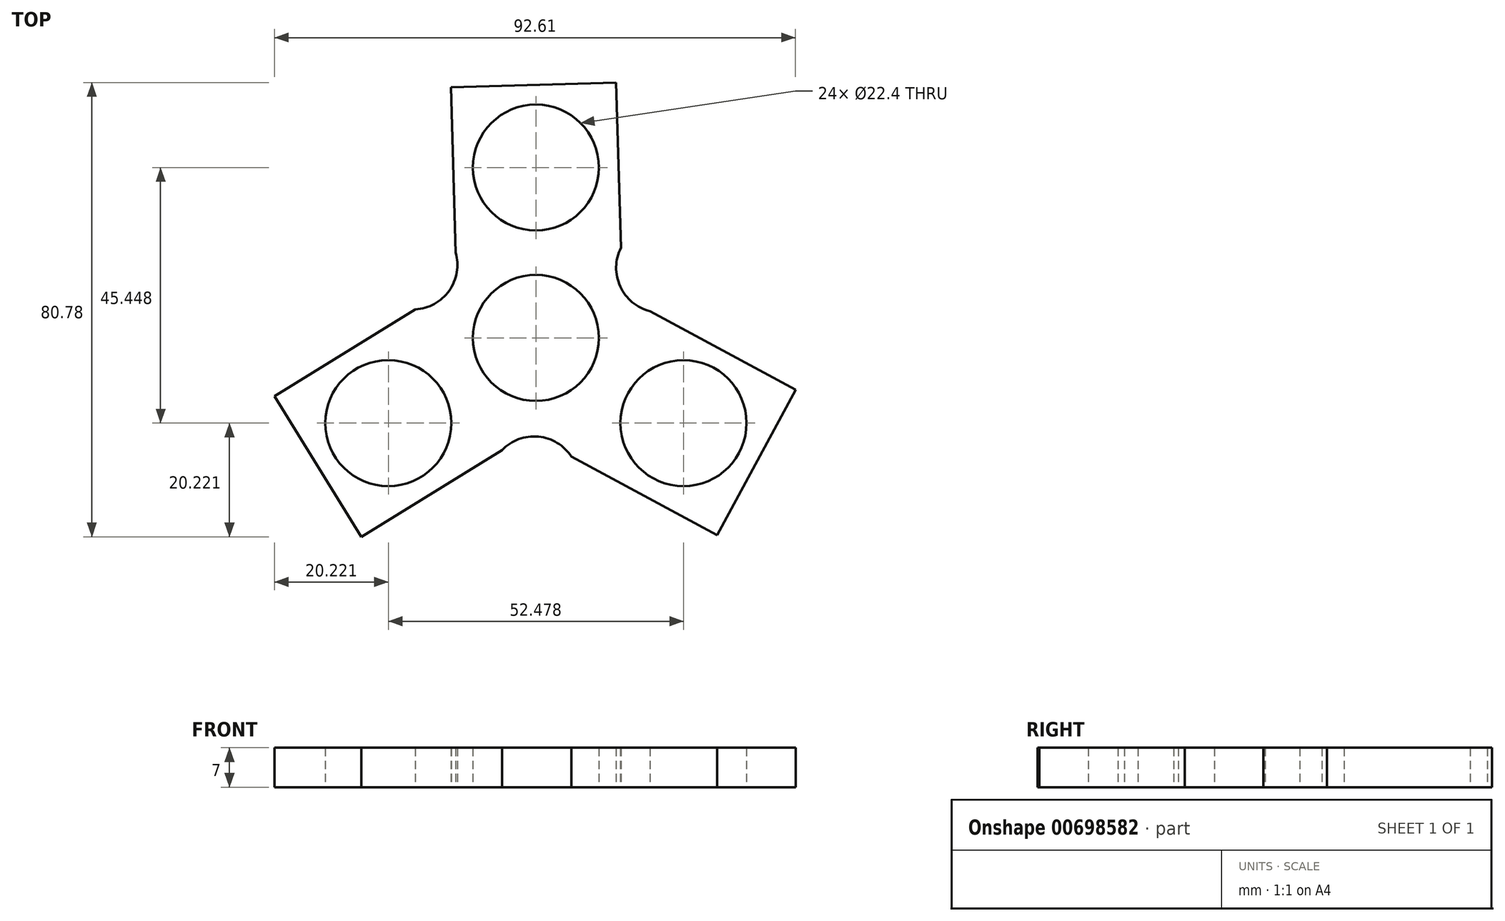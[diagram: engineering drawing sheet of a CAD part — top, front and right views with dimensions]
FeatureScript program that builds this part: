
annotation { "Feature Type Name" : "Feature", "Feature Type Description" : "" }
export const myFeature = defineFeature(function(context is Context, id is Id, definition is map)
    precondition{}
    {
        {
            var Q0;
            Q0=qCreatedBy(makeId("Top.planeOp"),FACE);
            var sketch = newSketch(context, id + "F0", { "sketchPlane" : qUnion([Q0])});
            skCircle(sketch, "E0", {"center": v(0, 0) * mm, "radius": 11.2 * mm});
            skCircle(sketch, "E1", {"center": v(0, 30.3) * mm, "radius": 11.2 * mm});
            skLineSegment(sketch, "E2.0", {"start": v(-15.12, 44.56) * mm, "end": v(14.27, 45.41) * mm});
            skLineSegment(sketch, "E2.1", {"start": v(14.27, 45.41) * mm, "end": v(15.12, 16.03) * mm});
            skLineSegment(sketch, "E2.3", {"start": v(-14.27, 15.18) * mm, "end": v(-15.12, 44.56) * mm});
            skPoint(sketch, "E2.0.midPoint", {"position": v(-0.43, 44.99) * mm});
            skCircle(sketch, "E3.1.0", {"center": v(-26.24, -15.15) * mm, "radius": 11.2 * mm});
            skLineSegment(sketch, "E3.1.2", {"start": v(-6.02, -19.95) * mm, "end": v(-31.04, -35.37) * mm});
            skLineSegment(sketch, "E3.1.3", {"start": v(-31.04, -35.37) * mm, "end": v(-46.46, -10.35) * mm});
            skLineSegment(sketch, "E3.1.4", {"start": v(-46.46, -10.35) * mm, "end": v(-21.44, 5.07) * mm});
            skCircle(sketch, "E3.2.0", {"center": v(26.24, -15.15) * mm, "radius": 11.2 * mm});
            skLineSegment(sketch, "E3.2.2", {"start": v(20.28, 4.76) * mm, "end": v(46.15, -9.2) * mm});
            skLineSegment(sketch, "E3.2.3", {"start": v(46.15, -9.2) * mm, "end": v(32.2, -35.06) * mm});
            skLineSegment(sketch, "E3.2.4", {"start": v(32.2, -35.06) * mm, "end": v(6.33, -21.1) * mm});
            skArc(sketch, "E4", {"start": v(-21.44, 5.07) * mm, "mid": v(-15.42, 8.4) * mm, "end": v(-14.27, 15.18) * mm});
            skArc(sketch, "E5.1.0", {"start": v(6.33, -21.1) * mm, "mid": v(0.44, -17.55) * mm, "end": v(-6.02, -19.95) * mm});
            skArc(sketch, "E5.2.0", {"start": v(15.12, 16.03) * mm, "mid": v(14.98, 9.15) * mm, "end": v(20.28, 4.76) * mm});
            skSolve(sketch);
        }
        {
            var Q0;
            Q0=makeQuery(id+"F0.imprint","IMPRINT",FACE,{"disambiguationData":[TD([[makeQuery(id+"F0.imprint","IMPRINT",EDGE,{"derivedFrom":sQuery(id+"F0.wireOp",EDGE,"E0")}),-1.0]])]});
            extrude(context, id + "F1", {"entities" : qUnion([Q0]), "depth" : 7 * mm, "offsetDistance" : 25 * mm});
        }
    });
